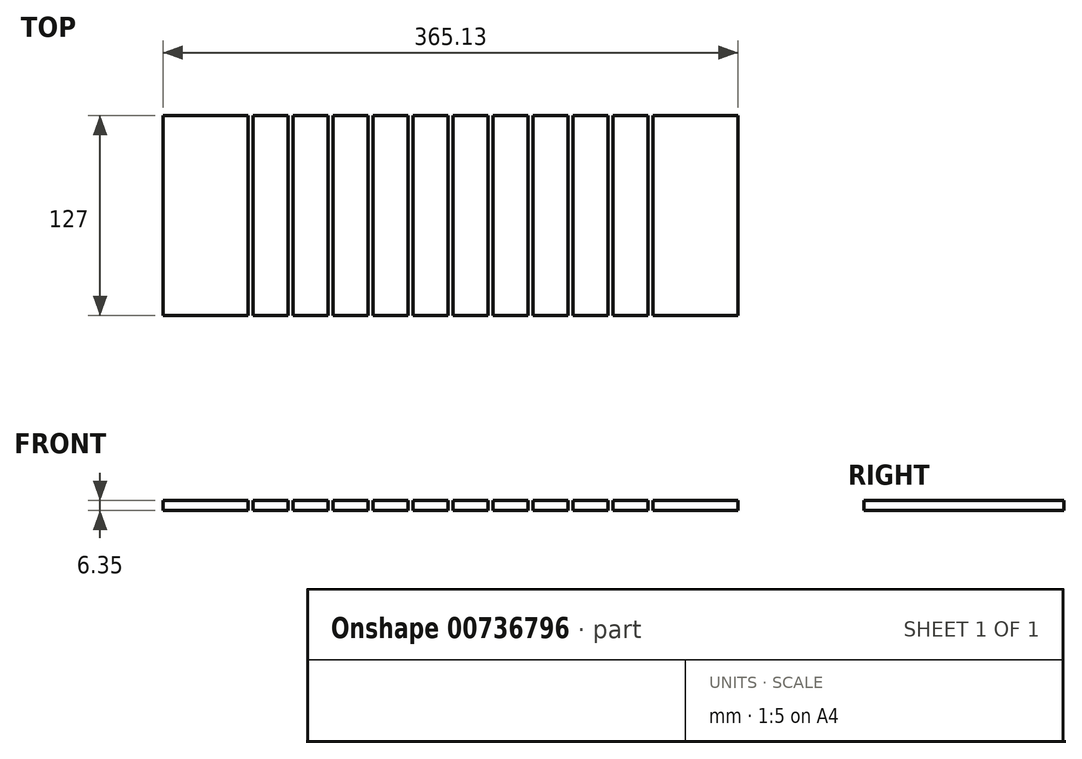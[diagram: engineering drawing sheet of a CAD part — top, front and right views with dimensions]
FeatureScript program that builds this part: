
annotation { "Feature Type Name" : "Feature", "Feature Type Description" : "" }
export const myFeature = defineFeature(function(context is Context, id is Id, definition is map)
    precondition{}
    {
        {
            var Q0;
            Q0=qCreatedBy(makeId("Top.planeOp"),FACE);
            var sketch = newSketch(context, id + "F0", { "sketchPlane" : qUnion([Q0])});
            skLineSegment(sketch, "E0.bottom", {"start": v(-158.75, 70.68) * mm, "end": v(-104.77, 70.68) * mm});
            skLineSegment(sketch, "E0.top", {"start": v(-158.75, -56.32) * mm, "end": v(-104.77, -56.32) * mm});
            skLineSegment(sketch, "E0.left", {"start": v(-158.75, 70.68) * mm, "end": v(-158.75, -56.32) * mm});
            skLineSegment(sketch, "E0.right", {"start": v(-104.77, 70.68) * mm, "end": v(-104.77, -56.32) * mm});
            skLineSegment(sketch, "E1.bottom", {"start": v(-101.6, 70.68) * mm, "end": v(-79.38, 70.68) * mm});
            skLineSegment(sketch, "E1.top", {"start": v(-101.6, -56.32) * mm, "end": v(-79.38, -56.32) * mm});
            skLineSegment(sketch, "E1.left", {"start": v(-101.6, 70.68) * mm, "end": v(-101.6, -56.32) * mm});
            skLineSegment(sketch, "E1.right", {"start": v(-79.38, 70.68) * mm, "end": v(-79.38, -56.32) * mm});
            skLineSegment(sketch, "E2.bottom", {"start": v(-76.2, 70.68) * mm, "end": v(-53.98, 70.68) * mm});
            skLineSegment(sketch, "E2.top", {"start": v(-76.2, -56.32) * mm, "end": v(-53.97, -56.32) * mm});
            skLineSegment(sketch, "E2.left", {"start": v(-76.2, 70.68) * mm, "end": v(-76.2, -56.32) * mm});
            skLineSegment(sketch, "E2.right", {"start": v(-53.98, 70.68) * mm, "end": v(-53.97, -56.32) * mm});
            skLineSegment(sketch, "E3.bottom", {"start": v(-50.8, 70.68) * mm, "end": v(-28.58, 70.68) * mm});
            skLineSegment(sketch, "E3.top", {"start": v(-50.8, -56.32) * mm, "end": v(-28.57, -56.32) * mm});
            skLineSegment(sketch, "E3.left", {"start": v(-50.8, 70.68) * mm, "end": v(-50.8, -56.32) * mm});
            skLineSegment(sketch, "E3.right", {"start": v(-28.58, 70.68) * mm, "end": v(-28.57, -56.32) * mm});
            skLineSegment(sketch, "E4.bottom", {"start": v(-25.4, 70.68) * mm, "end": v(-3.18, 70.68) * mm});
            skLineSegment(sketch, "E4.top", {"start": v(-25.4, -56.32) * mm, "end": v(-3.17, -56.32) * mm});
            skLineSegment(sketch, "E4.left", {"start": v(-25.4, 70.68) * mm, "end": v(-25.4, -56.32) * mm});
            skLineSegment(sketch, "E4.right", {"start": v(-3.18, 70.68) * mm, "end": v(-3.17, -56.32) * mm});
            skLineSegment(sketch, "E5.bottom", {"start": v(0, 70.68) * mm, "end": v(22.22, 70.68) * mm});
            skLineSegment(sketch, "E5.top", {"start": v(0, -56.32) * mm, "end": v(22.23, -56.32) * mm});
            skLineSegment(sketch, "E5.left", {"start": v(0, 70.68) * mm, "end": v(0, -56.32) * mm});
            skLineSegment(sketch, "E5.right", {"start": v(22.22, 70.68) * mm, "end": v(22.23, -56.32) * mm});
            skLineSegment(sketch, "E6.bottom", {"start": v(25.4, 70.68) * mm, "end": v(47.62, 70.68) * mm});
            skLineSegment(sketch, "E6.top", {"start": v(25.4, -56.32) * mm, "end": v(47.63, -56.32) * mm});
            skLineSegment(sketch, "E6.left", {"start": v(25.4, 70.68) * mm, "end": v(25.4, -56.32) * mm});
            skLineSegment(sketch, "E6.right", {"start": v(47.62, 70.68) * mm, "end": v(47.63, -56.32) * mm});
            skLineSegment(sketch, "E7.bottom", {"start": v(50.8, 70.68) * mm, "end": v(73.03, 70.68) * mm});
            skLineSegment(sketch, "E7.top", {"start": v(50.8, -56.32) * mm, "end": v(73.03, -56.32) * mm});
            skLineSegment(sketch, "E7.left", {"start": v(50.8, 70.68) * mm, "end": v(50.8, -56.32) * mm});
            skLineSegment(sketch, "E7.right", {"start": v(73.03, 70.68) * mm, "end": v(73.03, -56.32) * mm});
            skLineSegment(sketch, "E8.bottom", {"start": v(76.2, 70.68) * mm, "end": v(98.43, 70.68) * mm});
            skLineSegment(sketch, "E8.top", {"start": v(76.2, -56.32) * mm, "end": v(98.43, -56.32) * mm});
            skLineSegment(sketch, "E8.left", {"start": v(76.2, 70.68) * mm, "end": v(76.2, -56.32) * mm});
            skLineSegment(sketch, "E8.right", {"start": v(98.43, 70.68) * mm, "end": v(98.43, -56.32) * mm});
            skLineSegment(sketch, "E9.bottom", {"start": v(101.6, 70.68) * mm, "end": v(123.83, 70.68) * mm});
            skLineSegment(sketch, "E9.top", {"start": v(101.6, -56.32) * mm, "end": v(123.83, -56.32) * mm});
            skLineSegment(sketch, "E9.left", {"start": v(101.6, 70.68) * mm, "end": v(101.6, -56.32) * mm});
            skLineSegment(sketch, "E9.right", {"start": v(123.83, 70.68) * mm, "end": v(123.83, -56.32) * mm});
            skLineSegment(sketch, "E10.bottom", {"start": v(127, 70.68) * mm, "end": v(149.23, 70.68) * mm});
            skLineSegment(sketch, "E10.top", {"start": v(127, -56.32) * mm, "end": v(149.23, -56.32) * mm});
            skLineSegment(sketch, "E10.left", {"start": v(127, 70.68) * mm, "end": v(127, -56.32) * mm});
            skLineSegment(sketch, "E10.right", {"start": v(149.23, 70.68) * mm, "end": v(149.23, -56.32) * mm});
            skLineSegment(sketch, "E11.bottom", {"start": v(152.4, 70.68) * mm, "end": v(206.38, 70.68) * mm});
            skLineSegment(sketch, "E11.top", {"start": v(152.4, -56.32) * mm, "end": v(206.38, -56.32) * mm});
            skLineSegment(sketch, "E11.left", {"start": v(152.4, 70.68) * mm, "end": v(152.4, -56.32) * mm});
            skLineSegment(sketch, "E11.right", {"start": v(206.38, 70.68) * mm, "end": v(206.38, -56.32) * mm});
            skLineSegment(sketch, "E12", {"start": v(-158.75, 58.14) * mm, "end": v(-104.77, 58.14) * mm});
            skSolve(sketch);
        }
        {
            var Q0;
            {var subQ0=sQuery(id+"F0.wireOp",EDGE,"E0.bottom");Q0=makeQuery(id+"F0.imprint","IMPRINT",FACE,{"disambiguationData":[TD([[makeQuery(id+"F0.imprint","IMPRINT",EDGE,{"derivedFrom":subQ0}),-1.0]])]});}
            var Q1;
            {var subQ0=sQuery(id+"F0.wireOp",EDGE,"E0.top");Q1=makeQuery(id+"F0.imprint","IMPRINT",FACE,{"disambiguationData":[TD([[makeQuery(id+"F0.imprint","IMPRINT",EDGE,{"derivedFrom":subQ0}),1.0]])]});}
            var Q2;
            Q2=makeQuery(id+"F0.imprint","IMPRINT",FACE,{"disambiguationData":[TD([[makeQuery(id+"F0.imprint","IMPRINT",EDGE,{"derivedFrom":sQuery(id+"F0.wireOp",EDGE,"E1.bottom")}),-1.0]])]});
            var Q3;
            Q3=makeQuery(id+"F0.imprint","IMPRINT",FACE,{"disambiguationData":[TD([[makeQuery(id+"F0.imprint","IMPRINT",EDGE,{"derivedFrom":sQuery(id+"F0.wireOp",EDGE,"E2.bottom")}),-1.0]])]});
            var Q4;
            Q4=makeQuery(id+"F0.imprint","IMPRINT",FACE,{"disambiguationData":[TD([[makeQuery(id+"F0.imprint","IMPRINT",EDGE,{"derivedFrom":sQuery(id+"F0.wireOp",EDGE,"E3.bottom")}),-1.0]])]});
            var Q5;
            Q5=makeQuery(id+"F0.imprint","IMPRINT",FACE,{"disambiguationData":[TD([[makeQuery(id+"F0.imprint","IMPRINT",EDGE,{"derivedFrom":sQuery(id+"F0.wireOp",EDGE,"E4.bottom")}),-1.0]])]});
            var Q6;
            Q6=makeQuery(id+"F0.imprint","IMPRINT",FACE,{"disambiguationData":[TD([[makeQuery(id+"F0.imprint","IMPRINT",EDGE,{"derivedFrom":sQuery(id+"F0.wireOp",EDGE,"E5.bottom")}),-1.0]])]});
            var Q7;
            Q7=makeQuery(id+"F0.imprint","IMPRINT",FACE,{"disambiguationData":[TD([[makeQuery(id+"F0.imprint","IMPRINT",EDGE,{"derivedFrom":sQuery(id+"F0.wireOp",EDGE,"E6.bottom")}),-1.0]])]});
            var Q8;
            Q8=makeQuery(id+"F0.imprint","IMPRINT",FACE,{"disambiguationData":[TD([[makeQuery(id+"F0.imprint","IMPRINT",EDGE,{"derivedFrom":sQuery(id+"F0.wireOp",EDGE,"E7.bottom")}),-1.0]])]});
            var Q9;
            Q9=makeQuery(id+"F0.imprint","IMPRINT",FACE,{"disambiguationData":[TD([[makeQuery(id+"F0.imprint","IMPRINT",EDGE,{"derivedFrom":sQuery(id+"F0.wireOp",EDGE,"E8.bottom")}),-1.0]])]});
            var Q10;
            Q10=makeQuery(id+"F0.imprint","IMPRINT",FACE,{"disambiguationData":[TD([[makeQuery(id+"F0.imprint","IMPRINT",EDGE,{"derivedFrom":sQuery(id+"F0.wireOp",EDGE,"E9.bottom")}),-1.0]])]});
            var Q11;
            Q11=makeQuery(id+"F0.imprint","IMPRINT",FACE,{"disambiguationData":[TD([[makeQuery(id+"F0.imprint","IMPRINT",EDGE,{"derivedFrom":sQuery(id+"F0.wireOp",EDGE,"E10.bottom")}),-1.0]])]});
            var Q12;
            Q12=makeQuery(id+"F0.imprint","IMPRINT",FACE,{"disambiguationData":[TD([[makeQuery(id+"F0.imprint","IMPRINT",EDGE,{"derivedFrom":sQuery(id+"F0.wireOp",EDGE,"E11.bottom")}),-1.0]])]});
            extrude(context, id + "F1", {"entities" : qUnion([Q0, Q1, Q2, Q3, Q4, Q5, Q6, Q7, Q8, Q9, Q10, Q11, Q12]), "depth" : 6.35 * mm, "offsetDistance" : 25.4 * mm});
        }
    });
